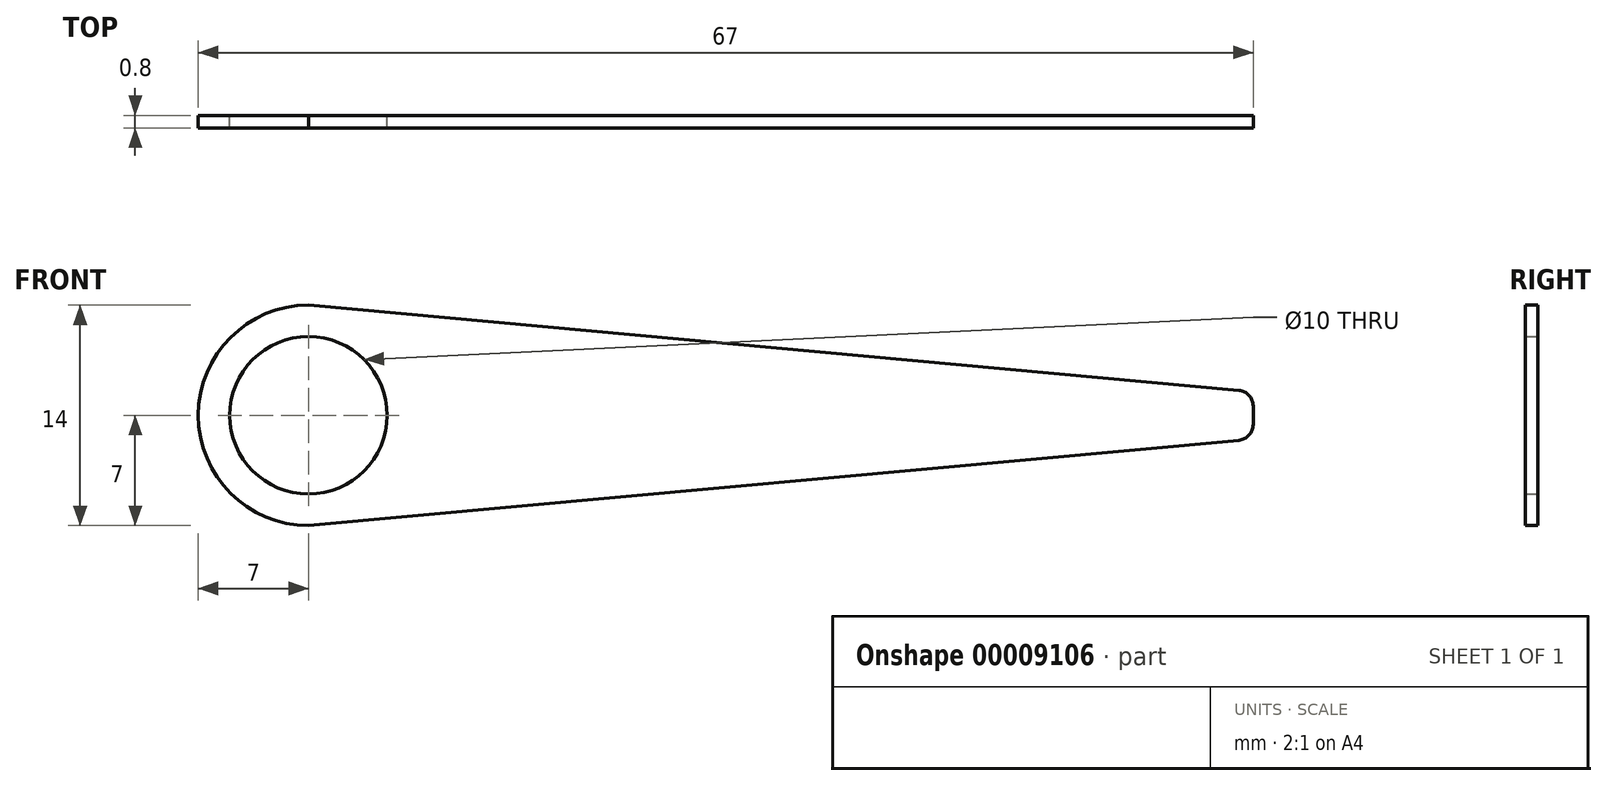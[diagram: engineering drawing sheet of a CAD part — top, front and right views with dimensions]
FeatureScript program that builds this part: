
annotation { "Feature Type Name" : "Feature", "Feature Type Description" : "" }
export const myFeature = defineFeature(function(context is Context, id is Id, definition is map)
    precondition{}
    {
        {
            var Q0;
            Q0=qCreatedBy(makeId("Front.planeOp"),FACE);
            var sketch = newSketch(context, id + "F0", { "sketchPlane" : qUnion([Q0])});
            skCircle(sketch, "E0", {"center": v(0, 0) * mm, "radius": 5 * mm});
            skCircle(sketch, "E1", {"center": v(0, 0) * mm, "radius": 7 * mm});
            skLineSegment(sketch, "E2", {"start": v(0, 7) * mm, "end": v(60, 1.5) * mm});
            skLineSegment(sketch, "E3", {"start": v(60, 1.5) * mm, "end": v(60, 0) * mm});
            skLineSegment(sketch, "E4.MirrorCS", {"start": v(0, -7) * mm, "end": v(60, -1.5) * mm});
            skLineSegment(sketch, "E5.MirrorCS", {"start": v(60, -1.5) * mm, "end": v(60, 0) * mm});
            skSolve(sketch);
        }
        {
            var Q0;
            Q0=makeQuery(id+"F0.imprint","IMPRINT",FACE,{"disambiguationData":[TD([[makeQuery(id+"F0.imprint","IMPRINT",EDGE,{"derivedFrom":sQuery(id+"F0.wireOp",EDGE,"E0")}),-1.0]])]});
            var Q1;
            {var subQ4=sQuery(id+"F0.wireOp",EDGE,"E3");Q1=makeQuery(id+"F0.imprint","IMPRINT",FACE,{"disambiguationData":[TD([[makeQuery(id+"F0.imprint","IMPRINT",EDGE,{"derivedFrom":subQ4}),-1.0]])]});}
            extrude(context, id + "F1", {"entities" : qUnion([Q0, Q1]), "depth" : 0.8 * mm});
        }
        {
            var Q0;
            Q0=makeQuery(id+"F1.opExtrude","CAP_FACE",FACE,{"disambiguationData":[OSD([sQuery(id+"F0.wireOp",EDGE,"E0"),sQuery(id+"F0.wireOp",EDGE,"E1"),sQuery(id+"F0.wireOp",EDGE,"E2"),sQuery(id+"F0.wireOp",EDGE,"E3"),sQuery(id+"F0.wireOp",EDGE,"E4.MirrorCS"),sQuery(id+"F0.wireOp",EDGE,"E5.MirrorCS")])],"isStart":false});
            var sketch = newSketch(context, id + "F2", { "sketchPlane" : qUnion([Q0])});
            skLineSegment(sketch, "E6.0.0", {"start": v(60, 1.5) * mm, "end": v(0, 7) * mm});
            skArc(sketch, "E6.0.1", {"start": v(0, 7) * mm, "mid": v(-7, 0) * mm, "end": v(0, -7) * mm});
            skLineSegment(sketch, "E6.0.2", {"start": v(0, -7) * mm, "end": v(60, -1.5) * mm});
            skLineSegment(sketch, "E6.0.3", {"start": v(60, -1.5) * mm, "end": v(60, 1.5) * mm});
            skLineSegment(sketch, "E7.0", {"start": v(43.5, 0) * mm, "end": v(-0.27, 4.01) * mm});
            skLineSegment(sketch, "E7.1", {"start": v(-0.27, -4.01) * mm, "end": v(43.5, 0) * mm});
            skCircle(sketch, "E8", {"center": v(0, 0) * mm, "radius": 9 * mm});
            skSolve(sketch);
        }
        {
            var Q0;
            Q0=makeQuery(id+"FFWXDJsPs1W2YDB_1.boolean.opBoolean","COPY",EDGE,{"derivedFrom":makeQuery(id+"FFWXDJsPs1W2YDB_1.opExtrude","SWEPT_EDGE",EDGE,{"disambiguationData":[OSD([sQuery(id+"F2.wireOp",EDGE,"E7.0"),sQuery(id+"F2.wireOp",EDGE,"E8")])]})});
            var Q1;
            Q1=makeQuery(id+"FFWXDJsPs1W2YDB_1.boolean.opBoolean","COPY",EDGE,{"derivedFrom":makeQuery(id+"FFWXDJsPs1W2YDB_1.opExtrude","SWEPT_EDGE",EDGE,{"disambiguationData":[OSD([sQuery(id+"F2.wireOp",EDGE,"E7.1"),sQuery(id+"F2.wireOp",EDGE,"E8")])]})});
            var Q2;
            Q2=makeQuery(id+"FFWXDJsPs1W2YDB_1.boolean.opBoolean","COPY",EDGE,{"derivedFrom":makeQuery(id+"FFWXDJsPs1W2YDB_1.opExtrude","SWEPT_EDGE",EDGE,{"disambiguationData":[OSD([sQuery(id+"F2.wireOp",EDGE,"E7.0"),sQuery(id+"F2.wireOp",EDGE,"E7.1")])]})});
            var Q3;
            Q3=makeQuery(id+"F1.opExtrude","SWEPT_EDGE",EDGE,{"disambiguationData":[OSD([sQuery(id+"F0.wireOp",EDGE,"E2"),sQuery(id+"F0.wireOp",EDGE,"E3")])]});
            var Q4;
            Q4=makeQuery(id+"F1.opExtrude","SWEPT_EDGE",EDGE,{"disambiguationData":[OSD([sQuery(id+"F0.wireOp",EDGE,"E4.MirrorCS"),sQuery(id+"F0.wireOp",EDGE,"E5.MirrorCS")])]});
            fillet(context, id + "F3", {"entities" : qUnion([Q0, Q1, Q2, Q3, Q4]), "radius" : 1 * mm, "tangentPropagation" : true, "allowEdgeOverflow" : false});
        }
    });
